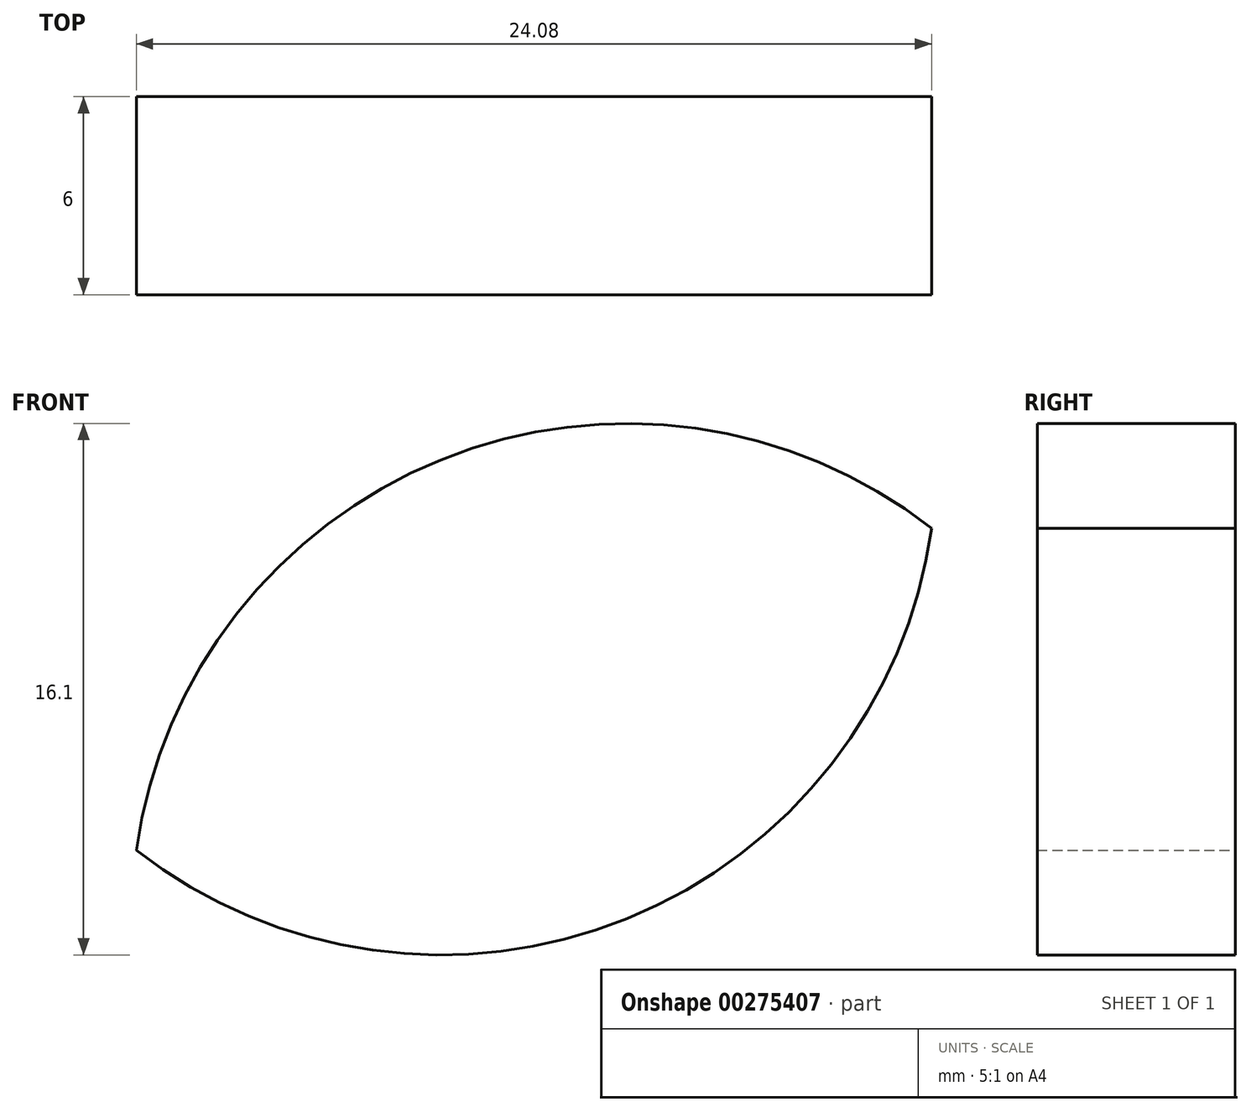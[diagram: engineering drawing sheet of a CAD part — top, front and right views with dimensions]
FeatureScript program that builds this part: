
annotation { "Feature Type Name" : "Feature", "Feature Type Description" : "" }
export const myFeature = defineFeature(function(context is Context, id is Id, definition is map)
    precondition{}
    {
        {
            var Q0;
            Q0=qCreatedBy(makeId("Front.planeOp"),FACE);
            var sketch = newSketch(context, id + "F0", { "sketchPlane" : qUnion([Q0])});
            skArc(sketch, "E0", {"start": v(-30.93, 9.76) * mm, "mid": v(-45.79, 11.83) * mm, "end": v(-55.01, 0) * mm});
            skArc(sketch, "E1", {"start": v(-55.01, 0) * mm, "mid": v(-40.15, -2.07) * mm, "end": v(-30.93, 9.76) * mm});
            skSolve(sketch);
        }
        {
            var Q0;
            Q0=sQuery(id+"F0.wireOp",EDGE,"48d13520-4469-4a7a-a7ec-f8db8a7fef93");
            var Q1;
            Q1=sQuery(id+"F0.wireOp",EDGE,"E0");
            var Q2;
            Q2=sQuery(id+"F0.wireOp",EDGE,"E1");
            var Q3;
            Q3=sQuery(id+"F0.wireOp",EDGE,"c6d5de4c-cbc5-4ef2-98c0-717be9272c6a");
            extrude(context, id + "F1", {"bodyType" : ToolBodyType.SURFACE, "surfaceEntities" : qUnion([Q0, Q1, Q2, Q3]), "depth" : 6 * mm, "offsetDistance" : 25 * mm});
        }
        {
            var Q0;
            Q0=makeQuery(id+"F0.imprint","IMPRINT",FACE,{"disambiguationData":[TD([[makeQuery(id+"F0.imprint","IMPRINT",EDGE,{"derivedFrom":sQuery(id+"F0.wireOp",EDGE,"E0")}),1.0]])]});
            var Q1;
            Q1=makeQuery(id+"F0.imprint","IMPRINT",FACE,{"disambiguationData":[TD([[makeQuery(id+"F0.imprint","IMPRINT",EDGE,{"derivedFrom":sQuery(id+"F0.wireOp",EDGE,"c6d5de4c-cbc5-4ef2-98c0-717be9272c6a")}),1.0]])]});
            extrude(context, id + "F2", {"entities" : qUnion([Q0, Q1]), "depth" : 6 * mm, "offsetDistance" : 25 * mm});
        }
    });
